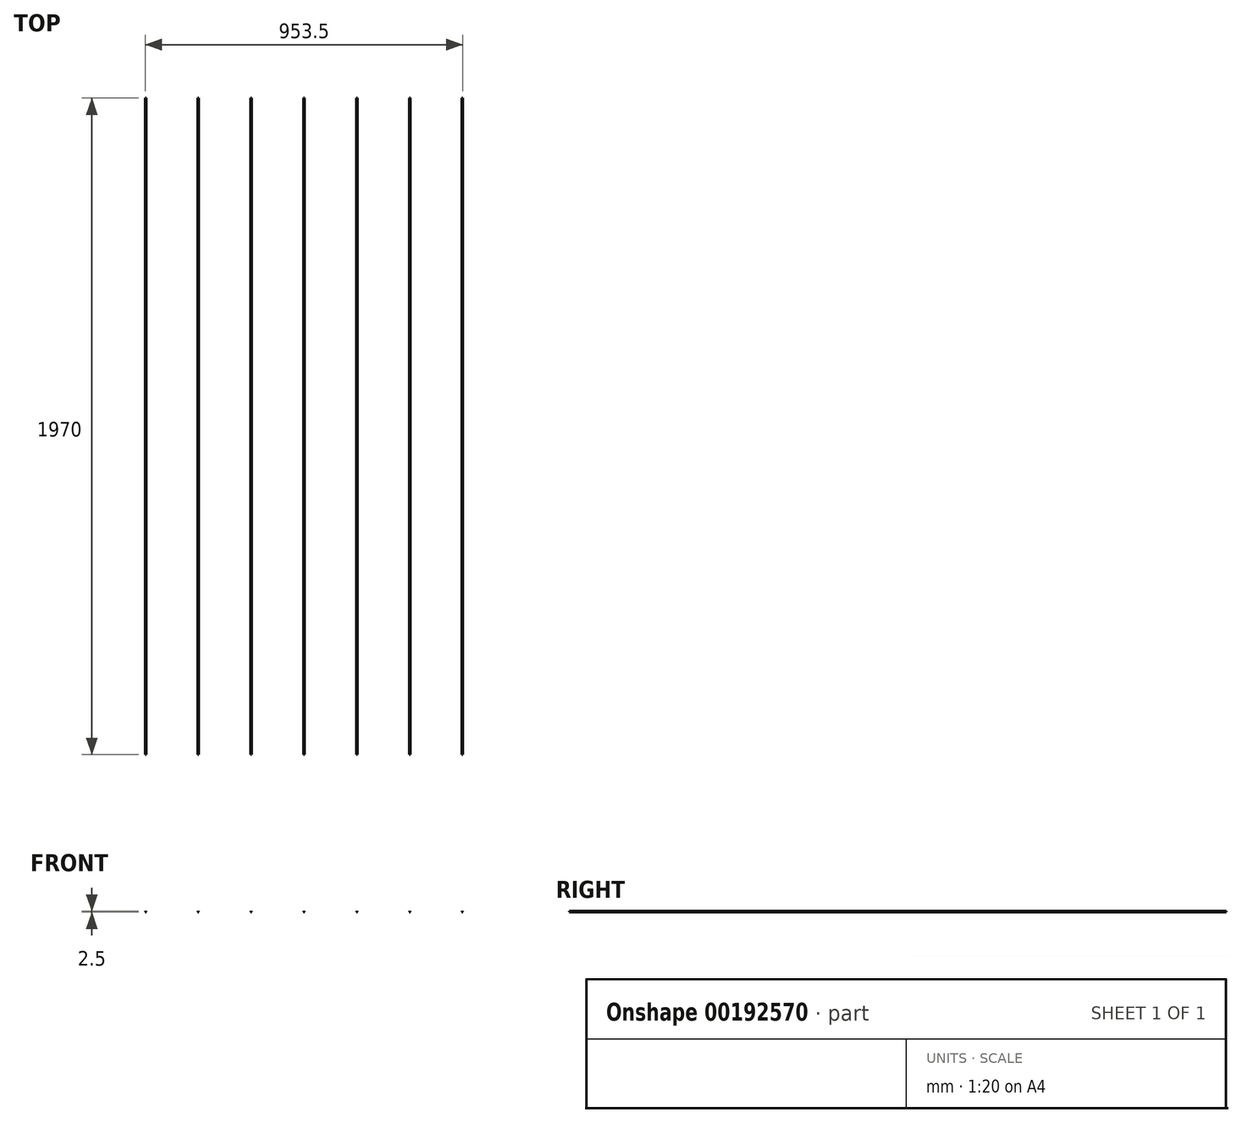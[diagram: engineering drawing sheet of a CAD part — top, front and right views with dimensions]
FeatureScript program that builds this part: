
annotation { "Feature Type Name" : "Feature", "Feature Type Description" : "" }
export const myFeature = defineFeature(function(context is Context, id is Id, definition is map)
    precondition{}
    {
        {
            var Q0;
            Q0=qCreatedBy(makeId("Front.planeOp"),FACE);
            var sketch = newSketch(context, id + "F0", { "sketchPlane" : qUnion([Q0])});
            skLineSegment(sketch, "E0", {"start": v(0, 0) * mm, "end": v(2.5, 0) * mm});
            skLineSegment(sketch, "E1", {"start": v(2.5, 0) * mm, "end": v(1.25, 2.5) * mm});
            skLineSegment(sketch, "E2", {"start": v(1.25, 2.5) * mm, "end": v(0, 0) * mm});
            skLineSegment(sketch, "E3.1.0.0", {"start": v(161, 0) * mm, "end": v(159.75, 2.5) * mm});
            skLineSegment(sketch, "E3.1.0.1", {"start": v(159.75, 2.5) * mm, "end": v(158.5, 0) * mm});
            skLineSegment(sketch, "E3.1.0.2", {"start": v(158.5, 0) * mm, "end": v(161, 0) * mm});
            skLineSegment(sketch, "E3.2.0.0", {"start": v(319.5, 0) * mm, "end": v(318.25, 2.5) * mm});
            skLineSegment(sketch, "E3.2.0.1", {"start": v(318.25, 2.5) * mm, "end": v(317, 0) * mm});
            skLineSegment(sketch, "E3.2.0.2", {"start": v(317, 0) * mm, "end": v(319.5, 0) * mm});
            skLineSegment(sketch, "E3.3.0.0", {"start": v(478, 0) * mm, "end": v(476.75, 2.5) * mm});
            skLineSegment(sketch, "E3.3.0.1", {"start": v(476.75, 2.5) * mm, "end": v(475.5, 0) * mm});
            skLineSegment(sketch, "E3.3.0.2", {"start": v(475.5, 0) * mm, "end": v(478, 0) * mm});
            skLineSegment(sketch, "E3.4.0.0", {"start": v(636.5, 0) * mm, "end": v(635.25, 2.5) * mm});
            skLineSegment(sketch, "E3.4.0.1", {"start": v(635.25, 2.5) * mm, "end": v(634, 0) * mm});
            skLineSegment(sketch, "E3.4.0.2", {"start": v(634, 0) * mm, "end": v(636.5, 0) * mm});
            skLineSegment(sketch, "E3.5.0.0", {"start": v(795, 0) * mm, "end": v(793.75, 2.5) * mm});
            skLineSegment(sketch, "E3.5.0.1", {"start": v(793.75, 2.5) * mm, "end": v(792.5, 0) * mm});
            skLineSegment(sketch, "E3.5.0.2", {"start": v(792.5, 0) * mm, "end": v(795, 0) * mm});
            skLineSegment(sketch, "E3.6.0.0", {"start": v(953.5, 0) * mm, "end": v(952.25, 2.5) * mm});
            skLineSegment(sketch, "E3.6.0.1", {"start": v(952.25, 2.5) * mm, "end": v(951, 0) * mm});
            skLineSegment(sketch, "E3.6.0.2", {"start": v(951, 0) * mm, "end": v(953.5, 0) * mm});
            skLineSegment(sketch, "E3.direction1", {"start": v(2.5, 0) * mm, "end": v(161, 0) * mm, "construction": true});
            skSolve(sketch);
        }
        {
            var Q0;
            Q0=makeQuery(id+"F0.imprint","IMPRINT",FACE,{"disambiguationData":[TD([[makeQuery(id+"F0.imprint","IMPRINT",EDGE,{"derivedFrom":sQuery(id+"F0.wireOp",EDGE,"E0")}),1.0]])]});
            extrude(context, id + "F1", {"entities" : qUnion([Q0]), "oppositeDirection" : true, "depth" : 1970 * mm});
        }
        {
            var Q0;
            Q0 = qSketchRegion(id + "F0", true);
            extrude(context, id + "F2", {"entities" : qUnion([Q0]), "operationType" : NewBodyOperationType.ADD, "oppositeDirection" : true, "depth" : 1970 * mm});
        }
    });
